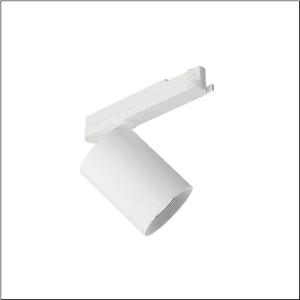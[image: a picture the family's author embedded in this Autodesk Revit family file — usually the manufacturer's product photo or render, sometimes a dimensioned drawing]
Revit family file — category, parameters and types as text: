
# Revit family: spot_21_51se13dbb5b
name_source: partatom
category: Lighting Fixtures
units: mm (PartAtom-declared; Revit-internal decimal feet)

## family parameters
Cut with Voids When Loaded = No
Host = Face
Light Source = No
Part Type = Normal
Room Calculation Point = No
Round Connector Dimension = Use Diameter
Shared = No

## types (1)
- --- (1 x LED, 5160 lm, 42.4 W, 3000K)
    Apparent Load = 42 VA
    CIE Flux Codes = 95 98 99 100 100
    Color Rendering = 90
    Color Temperature = 3000K
    Default Elevation = 1800 mm
    Description = Spot 21, directional spotlight, light control with lens, of PMMA, LED rated luminous flux: 5.120lm, light colour: 930, control gear: ECG Multilumen, with 3-phase adapter, mains connection: 220..240V, AC, 50/60Hz, of aluminium, traffic white (RAL 9016), length: 253mm, diameter: 105mm, protection rating (complete): IP20, insulation class (complete): insulation class I (protective earthing), certification: CE, impact resistance: IK02, permissible ambient temperature for indoor applications: -20..+40°C, packaging unit: 1 piece
    Height = 175 mm
    Lamp = 1 x LED
    Lamp Light Flux = 5160 lm
    Lamp Power = 42.4 W
    Lamp count = 1
    Length = 105 mm
    Luminous efficacy = 122 lm/W
    Manufacturer = Siteco
    ModVariant = No
    Model = 51SE13DBB5B
    Mounting Place = Ceiling
    Mounting Type = Pendant
    Number of Poles = 1
    OnlyDefault = Yes
    Power Factor = 1
    Product Name = Spot 21
    Product group = directional spotlight
    ProductGroupID = 905
    Protection Class = Protection class I
    Protection Degree = IP 20
    RLX_Detail_Level = 1
    RLX_Emergency_Light_Flux = 0 lm
    RLX_Emergency_Type = 0
    RLX_Emergency_Type_DB = No
    RlxData = <blob elided: 17681 chars, md5=2beffb61>
    Socket = socket
    Standby Power = 0 W
    System Light Flux = 5160 lm
    System Power = 42 W
    Type Comments = factory setting: luminous flux: 100 % | (ON | ON | ON | ON) | 1050 mA
    Type Image = l_1003976.jpg
    URL = http://relux.com
    VarID = @adj_093617
    Voltage = 0 V
    Weight = 0.00 kg
    Width = 0 mm  [stored 0 ft]

note: [stored X ft] marks values corroborated as IEEE doubles in the binary element streams (Revit-internal decimal feet)

## geometry (parser evidence)
native form markers: Blend x4, Sweep x8
no freeform markers — native parametric forms only
